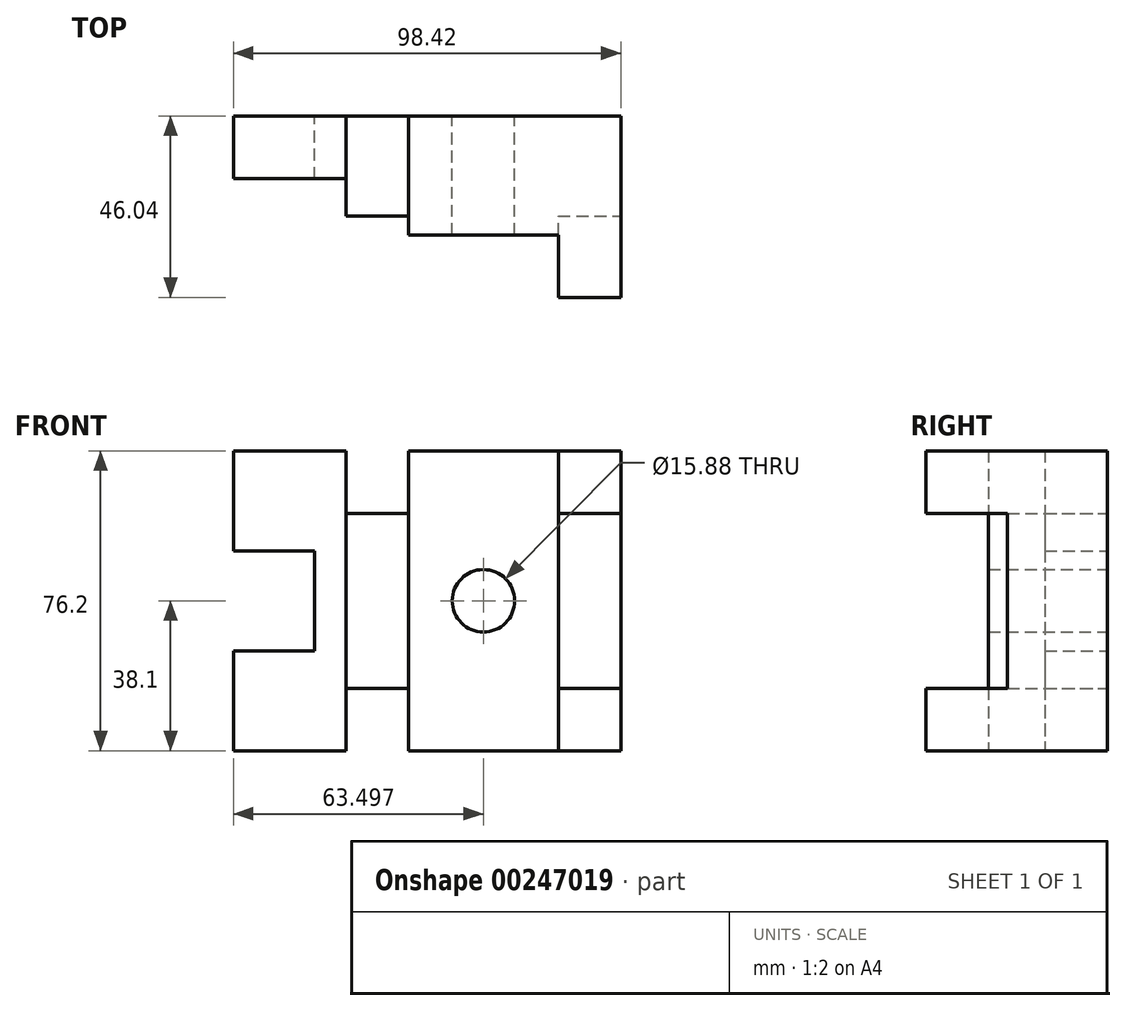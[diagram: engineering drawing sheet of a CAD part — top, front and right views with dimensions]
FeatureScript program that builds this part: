
annotation { "Feature Type Name" : "Feature", "Feature Type Description" : "" }
export const myFeature = defineFeature(function(context is Context, id is Id, definition is map)
    precondition{}
    {
        {
            var Q0;
            Q0=qCreatedBy(makeId("Front.planeOp"),FACE);
            var sketch = newSketch(context, id + "F0", { "sketchPlane" : qUnion([Q0])});
            skLineSegment(sketch, "E0.bottom", {"start": v(-56.7, 50.8) * mm, "end": v(70.3, 50.8) * mm});
            skLineSegment(sketch, "E0.top", {"start": v(-56.7, -25.4) * mm, "end": v(70.3, -25.4) * mm});
            skLineSegment(sketch, "E0.left", {"start": v(-56.7, 50.8) * mm, "end": v(-56.7, -25.4) * mm});
            skLineSegment(sketch, "E0.right", {"start": v(70.3, 50.8) * mm, "end": v(70.3, -25.4) * mm});
            skLineSegment(sketch, "E1", {"start": v(-36.06, 25.4) * mm, "end": v(-36.06, 0) * mm});
            skLineSegment(sketch, "E2", {"start": v(49.67, 25.4) * mm, "end": v(49.67, 0) * mm});
            skPoint(sketch, "E3", {"position": v(70.3, 25.4) * mm});
            skPoint(sketch, "E4", {"position": v(70.3, 0) * mm});
            skPoint(sketch, "E5", {"position": v(49.67, 25.4) * mm});
            skPoint(sketch, "E6", {"position": v(49.67, 0) * mm});
            skLineSegment(sketch, "E7", {"start": v(49.67, 25.4) * mm, "end": v(70.3, 25.4) * mm});
            skLineSegment(sketch, "E8", {"start": v(70.3, 0) * mm, "end": v(49.67, 0) * mm});
            skLineSegment(sketch, "E9", {"start": v(70.3, 25.4) * mm, "end": v(49.67, 25.4) * mm});
            skLineSegment(sketch, "E10", {"start": v(-56.7, 0) * mm, "end": v(-36.06, 0) * mm});
            skCircle(sketch, "E11", {"center": v(6.8, 12.7) * mm, "radius": 7.94 * mm});
            skPoint(sketch, "E12", {"position": v(-36.06, 34.92) * mm});
            skPoint(sketch, "E13", {"position": v(-36.06, -9.52) * mm});
            skPoint(sketch, "E14", {"position": v(-20.18, 34.92) * mm});
            skPoint(sketch, "E15", {"position": v(-20.18, -9.53) * mm});
            skPoint(sketch, "E16", {"position": v(33.8, -9.52) * mm});
            skPoint(sketch, "E17", {"position": v(49.67, -9.52) * mm});
            skPoint(sketch, "E18", {"position": v(33.8, 25.4) * mm});
            skPoint(sketch, "E19", {"position": v(33.8, 34.92) * mm});
            skPoint(sketch, "E20", {"position": v(49.67, 34.93) * mm});
            skPoint(sketch, "E21", {"position": v(33.8, 0) * mm});
            skPoint(sketch, "E22", {"position": v(-36.06, 25.4) * mm});
            skPoint(sketch, "E23", {"position": v(-20.18, 25.4) * mm});
            skPoint(sketch, "E24", {"position": v(-36.06, 0) * mm});
            skPoint(sketch, "E25", {"position": v(-20.18, 0) * mm});
            skLineSegment(sketch, "E26.left", {"start": v(70.3, 25.4) * mm, "end": v(70.3, 0) * mm});
            skLineSegment(sketch, "E27.bottom", {"start": v(-56.7, 25.4) * mm, "end": v(-36.06, 25.4) * mm});
            skLineSegment(sketch, "E27.left", {"start": v(-56.7, 25.4) * mm, "end": v(-56.7, 0) * mm});
            skLineSegment(sketch, "E28", {"start": v(41.73, 50.8) * mm, "end": v(41.73, -25.4) * mm});
            skLineSegment(sketch, "E29", {"start": v(-28.12, 50.8) * mm, "end": v(-28.12, -25.4) * mm});
            skLineSegment(sketch, "E30", {"start": v(25.86, 50.8) * mm, "end": v(25.86, -25.4) * mm});
            skLineSegment(sketch, "E31", {"start": v(-12.24, 50.8) * mm, "end": v(-12.24, -25.4) * mm});
            skPoint(sketch, "E32.orphan", {"position": v(-36.06, 50.8) * mm});
            skPoint(sketch, "E33.trimOffspring.end.orphan", {"position": v(-36.06, -25.4) * mm});
            skLineSegment(sketch, "E34.trimOffspring", {"start": v(-36.06, 25.4) * mm, "end": v(-56.7, 25.4) * mm});
            skPoint(sketch, "E35.orphan", {"position": v(49.67, 50.8) * mm});
            skPoint(sketch, "E36.orphan", {"position": v(-20.18, 50.8) * mm});
            skPoint(sketch, "E37.orphan", {"position": v(33.8, 50.8) * mm});
            skLineSegment(sketch, "E38.trimOffspring", {"start": v(49.67, 0) * mm, "end": v(70.3, 0) * mm});
            skPoint(sketch, "E39.orphan", {"position": v(49.67, -25.4) * mm});
            skPoint(sketch, "E40.trimOffspring.end.orphan", {"position": v(6.8, -25.4) * mm});
            skPoint(sketch, "E41.start.orphan", {"position": v(6.8, 50.8) * mm});
            skPoint(sketch, "E42.trimOffspring.end.orphan", {"position": v(70.3, 12.7) * mm});
            skPoint(sketch, "E43.start.orphan", {"position": v(-56.7, 12.7) * mm});
            skLineSegment(sketch, "E44", {"start": v(-28.12, 50.8) * mm, "end": v(-12.24, 50.8) * mm});
            skLineSegment(sketch, "E45", {"start": v(-28.12, -25.4) * mm, "end": v(-12.24, -25.4) * mm});
            skPoint(sketch, "E46", {"position": v(-28.12, -25.4) * mm});
            skPoint(sketch, "E47", {"position": v(-12.24, -25.4) * mm});
            skPoint(sketch, "E48", {"position": v(-56.7, 50.8) * mm});
            skPoint(sketch, "E49", {"position": v(-56.7, 25.4) * mm});
            skPoint(sketch, "E50", {"position": v(-56.7, 0) * mm});
            skPoint(sketch, "E51", {"position": v(-56.7, -25.4) * mm});
            skPoint(sketch, "E52", {"position": v(-28.12, 50.8) * mm});
            skPoint(sketch, "E53", {"position": v(41.73, 50.8) * mm});
            skPoint(sketch, "E54", {"position": v(41.73, -25.4) * mm});
            skPoint(sketch, "E55", {"position": v(70.3, -25.4) * mm});
            skPoint(sketch, "E56", {"position": v(70.3, 50.8) * mm});
            skLineSegment(sketch, "E57", {"start": v(-20.18, 34.92) * mm, "end": v(-12.24, 34.92) * mm});
            skLineSegment(sketch, "E58", {"start": v(-12.24, 34.92) * mm, "end": v(-28.12, 34.92) * mm});
            skLineSegment(sketch, "E59", {"start": v(-20.18, -9.53) * mm, "end": v(-28.12, -9.53) * mm});
            skLineSegment(sketch, "E60", {"start": v(-28.12, -9.53) * mm, "end": v(-12.24, -9.53) * mm});
            skLineSegment(sketch, "E61", {"start": v(33.8, 34.92) * mm, "end": v(25.86, 34.92) * mm});
            skLineSegment(sketch, "E62", {"start": v(25.86, 34.92) * mm, "end": v(41.73, 34.92) * mm});
            skLineSegment(sketch, "E63", {"start": v(33.8, -9.52) * mm, "end": v(25.86, -9.52) * mm});
            skLineSegment(sketch, "E64", {"start": v(25.86, -9.52) * mm, "end": v(41.73, -9.52) * mm});
            skPoint(sketch, "E65", {"position": v(-28.12, -9.53) * mm});
            skPoint(sketch, "E66", {"position": v(-12.24, -9.53) * mm});
            skPoint(sketch, "E67", {"position": v(-28.12, 34.92) * mm});
            skPoint(sketch, "E68", {"position": v(-12.24, 34.92) * mm});
            skPoint(sketch, "E69", {"position": v(25.86, 34.92) * mm});
            skPoint(sketch, "E70", {"position": v(41.73, 34.92) * mm});
            skPoint(sketch, "E71", {"position": v(25.86, 50.8) * mm});
            skPoint(sketch, "E72", {"position": v(25.86, -9.52) * mm});
            skPoint(sketch, "E73", {"position": v(41.73, -9.52) * mm});
            skPoint(sketch, "E74", {"position": v(25.86, -25.4) * mm});
            skLineSegment(sketch, "E75", {"start": v(-28.12, -9.53) * mm, "end": v(-28.12, -25.4) * mm});
            skLineSegment(sketch, "E76", {"start": v(-12.24, -25.4) * mm, "end": v(-28.12, -25.4) * mm});
            skSolve(sketch);
        }
        {
            var Q0;
            {var subQ4=sQuery(id+"F0.wireOp",EDGE,"E10");Q0=makeQuery(id+"F0.imprint","IMPRINT",FACE,{"disambiguationData":[TD([[makeQuery(id+"F0.imprint","IMPRINT",EDGE,{"derivedFrom":subQ4}),-1.0]])]});}
            var Q1;
            {var subQ7=sQuery(id+"F0.wireOp",EDGE,"E9");Q1=makeQuery(id+"F0.imprint","IMPRINT",FACE,{"disambiguationData":[TD([[makeQuery(id+"F0.imprint","IMPRINT",EDGE,{"derivedFrom":subQ7}),-1.0]])]});}
            extrude(context, id + "F1", {"entities" : qUnion([Q0, Q1]), "depth" : 15.88 * mm});
        }
        {
            var Q0;
            {var subQ4=sQuery(id+"F0.wireOp",EDGE,"E75");Q0=makeQuery(id+"F0.imprint","IMPRINT",FACE,{"disambiguationData":[TD([[makeQuery(id+"F0.imprint","IMPRINT",EDGE,{"derivedFrom":subQ4}),1.0]])]});}
            var Q1;
            {var subQ3=sQuery(id+"F0.wireOp",EDGE,"E62");var subQ5=makeQuery(id+"F0.imprint","IMPRINT",VERTEX,{"derivedFrom":subQ3});Q1=makeQuery(id+"F0.imprint","IMPRINT",FACE,{"disambiguationData":[TD([[makeQuery(id+"F0.imprint","IMPRINT",EDGE,{"disambiguationData":[TD([[subQ5,1.0]])],"derivedFrom":subQ3}),1.0]])]});}
            var Q2;
            {var subQ3=sQuery(id+"F0.wireOp",EDGE,"E64");var subQ5=makeQuery(id+"F0.imprint","IMPRINT",VERTEX,{"derivedFrom":subQ3});Q2=makeQuery(id+"F0.imprint","IMPRINT",FACE,{"disambiguationData":[TD([[makeQuery(id+"F0.imprint","IMPRINT",EDGE,{"disambiguationData":[TD([[subQ5,1.0]])],"derivedFrom":subQ3}),-1.0]])]});}
            var Q3;
            {var subQ4=sQuery(id+"F0.wireOp",EDGE,"E44");Q3=makeQuery(id+"F0.imprint","IMPRINT",FACE,{"disambiguationData":[TD([[makeQuery(id+"F0.imprint","IMPRINT",EDGE,{"derivedFrom":subQ4}),-1.0]])]});}
            extrude(context, id + "F2", {"entities" : qUnion([Q0, Q1, Q2, Q3]), "operationType" : NewBodyOperationType.ADD, "depth" : 46.04 * mm});
        }
        {
            var Q0;
            Q0=makeQuery(id+"F0.imprint","IMPRINT",FACE,{"disambiguationData":[TD([[makeQuery(id+"F0.imprint","IMPRINT",EDGE,{"derivedFrom":sQuery(id+"F0.wireOp",EDGE,"E11")}),-1.0]])]});
            extrude(context, id + "F3", {"entities" : qUnion([Q0]), "depth" : 30.16 * mm});
        }
        {
            var Q0;
            {var subQ0=sQuery(id+"F0.wireOp",EDGE,"E62");var subQ7=makeQuery(id+"F0.imprint","IMPRINT",VERTEX,{"derivedFrom":subQ0});Q0=makeQuery(id+"F0.imprint","IMPRINT",FACE,{"disambiguationData":[TD([[makeQuery(id+"F0.imprint","IMPRINT",EDGE,{"disambiguationData":[TD([[subQ7,1.0]])],"derivedFrom":subQ0}),-1.0]])]});}
            var Q1;
            {var subQ0=sQuery(id+"F0.wireOp",EDGE,"E58");var subQ3=makeQuery(id+"F0.imprint","IMPRINT",VERTEX,{"derivedFrom":subQ0});Q1=makeQuery(id+"F0.imprint","IMPRINT",FACE,{"disambiguationData":[TD([[makeQuery(id+"F0.imprint","IMPRINT",EDGE,{"disambiguationData":[TD([[subQ3,1.0]])],"derivedFrom":subQ0}),1.0]])]});}
            extrude(context, id + "F4", {"entities" : qUnion([Q0, Q1]), "operationType" : NewBodyOperationType.ADD, "depth" : 25.4 * mm});
        }
    });
